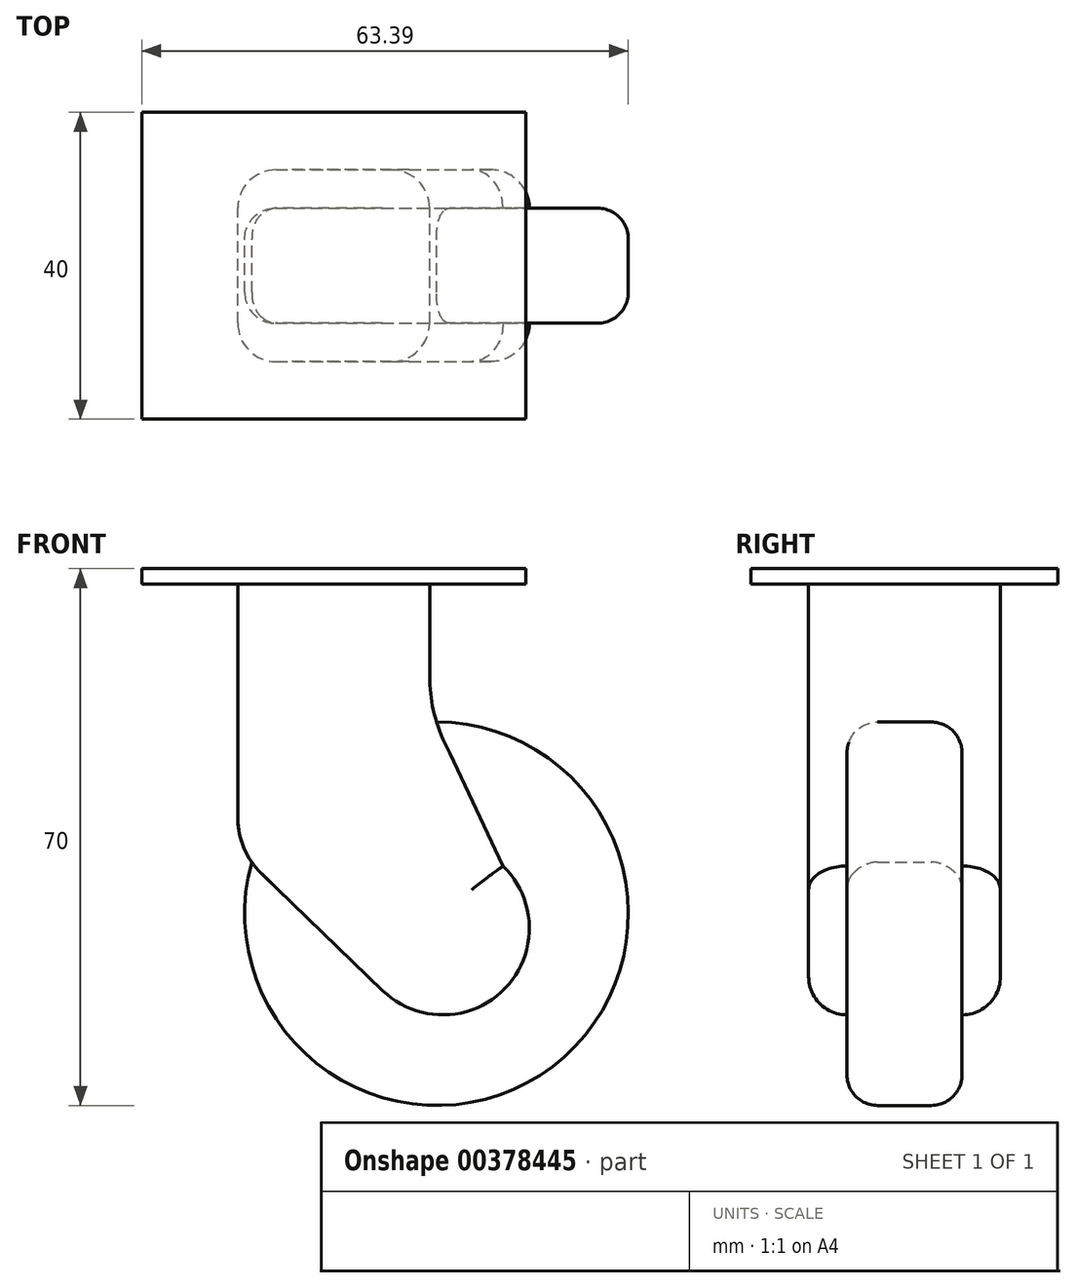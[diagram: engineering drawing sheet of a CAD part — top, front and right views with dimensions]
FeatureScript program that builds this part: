
annotation { "Feature Type Name" : "Feature", "Feature Type Description" : "" }
export const myFeature = defineFeature(function(context is Context, id is Id, definition is map)
    precondition{}
    {
        {
            var Q0;
            Q0=qCreatedBy(makeId("Top.planeOp"),FACE);
            var sketch = newSketch(context, id + "F0", { "sketchPlane" : qUnion([Q0])});
            skLineSegment(sketch, "E0.bottom", {"start": v(25, 20) * mm, "end": v(-25, 20) * mm});
            skLineSegment(sketch, "E0.top", {"start": v(25, -20) * mm, "end": v(-25, -20) * mm});
            skLineSegment(sketch, "E0.left", {"start": v(25, 20) * mm, "end": v(25, -20) * mm});
            skLineSegment(sketch, "E0.right", {"start": v(-25, 20) * mm, "end": v(-25, -20) * mm});
            skPoint(sketch, "E0.middle", {"position": v(0, 0) * mm});
            skSolve(sketch);
        }
        {
            var Q0;
            Q0=makeQuery(id+"F0.imprint","IMPRINT",FACE,{"disambiguationData":[TD([[makeQuery(id+"F0.imprint","IMPRINT",EDGE,{"derivedFrom":sQuery(id+"F0.wireOp",EDGE,"E0.bottom")}),1.0]])]});
            extrude(context, id + "F1", {"entities" : qUnion([Q0]), "depth" : 2 * mm});
        }
        {
            var Q0;
            Q0=qCreatedBy(makeId("Front.planeOp"),FACE);
            var sketch = newSketch(context, id + "F2", { "sketchPlane" : qUnion([Q0])});
            skLineSegment(sketch, "E1", {"start": v(-12.5, 0) * mm, "end": v(-12.5, -30.53) * mm});
            skLineSegment(sketch, "E2", {"start": v(12.5, 0) * mm, "end": v(12.5, -12.08) * mm});
            skLineSegment(sketch, "E3", {"start": v(14.42, -20.63) * mm, "end": v(22.05, -36.78) * mm});
            skLineSegment(sketch, "E4", {"start": v(6.35, -53) * mm, "end": v(-9.45, -37.71) * mm});
            skArc(sketch, "E5", {"start": v(6.35, -53) * mm, "mid": v(22.32, -52.75) * mm, "end": v(22.05, -36.78) * mm});
            skLineSegment(sketch, "E6", {"start": v(6.35, -53) * mm, "end": v(22.05, -36.78) * mm, "construction": true});
            skLineSegment(sketch, "E7", {"start": v(0, 0) * mm, "end": v(0, -14.48) * mm, "construction": true});
            skPoint(sketch, "E8.visualSharp", {"position": v(12.5, -16.57) * mm});
            skArc(sketch, "E8.filletArc", {"start": v(12.5, -12.08) * mm, "mid": v(12.99, -16.46) * mm, "end": v(14.42, -20.63) * mm});
            skPoint(sketch, "E9.visualSharp", {"position": v(-12.5, -34.77) * mm});
            skArc(sketch, "E9.filletArc", {"start": v(-12.5, -30.53) * mm, "mid": v(-11.7, -34.43) * mm, "end": v(-9.45, -37.71) * mm});
            skLineSegment(sketch, "E10", {"start": v(-12.5, 0) * mm, "end": v(12.5, 0) * mm});
            skSolve(sketch);
        }
        {
            var Q0;
            Q0=makeQuery(id+"F2.imprint","IMPRINT",FACE,{"disambiguationData":[TD([[makeQuery(id+"F2.imprint","IMPRINT",EDGE,{"derivedFrom":sQuery(id+"F2.wireOp",EDGE,"E1")}),1.0]])]});
            extrude(context, id + "F3", {"entities" : qUnion([Q0]), "operationType" : NewBodyOperationType.ADD, "endBound" : BoundingType.SYMMETRIC, "depth" : 25 * mm});
        }
        {
            var Q0;
            Q0=qCreatedBy(makeId("Front.planeOp"),FACE);
            var sketch = newSketch(context, id + "F4", { "sketchPlane" : qUnion([Q0])});
            skCircle(sketch, "E11", {"center": v(13.4, -43) * mm, "radius": 25 * mm});
            skSolve(sketch);
        }
        {
            var Q0;
            Q0=makeQuery(id+"F4.imprint","IMPRINT",FACE,{"disambiguationData":[TD([[makeQuery(id+"F4.imprint","IMPRINT",EDGE,{"derivedFrom":sQuery(id+"F4.wireOp",EDGE,"E11")}),1.0]])]});
            extrude(context, id + "F5", {"entities" : qUnion([Q0]), "operationType" : NewBodyOperationType.ADD, "endBound" : BoundingType.SYMMETRIC, "depth" : 15 * mm});
        }
        {
            var Q0;
            Q0=makeQuery(id+"F5.opExtrude","CAP_EDGE",EDGE,{"disambiguationData":[OSD([sQuery(id+"F4.wireOp",EDGE,"E11")])],"isStart":false});
            var Q1;
            Q1=makeQuery(id+"F5.opExtrude","CAP_EDGE",EDGE,{"disambiguationData":[OSD([sQuery(id+"F4.wireOp",EDGE,"E11")])],"isStart":true});
            fillet(context, id + "F6", {"entities" : qUnion([Q0, Q1]), "radius" : 4 * mm, "tangentPropagation" : true, "allowEdgeOverflow" : false});
        }
        {
            var Q0;
            Q0=makeQuery(id+"F3.opExtrude","CAP_EDGE",EDGE,{"disambiguationData":[OSD([sQuery(id+"F2.wireOp",EDGE,"E2")])],"isStart":false});
            var Q1;
            Q1=makeQuery(id+"F3.opExtrude","CAP_EDGE",EDGE,{"disambiguationData":[OSD([sQuery(id+"F2.wireOp",EDGE,"E1")])],"isStart":false});
            var Q2;
            Q2=makeQuery(id+"F3.opExtrude","CAP_EDGE",EDGE,{"disambiguationData":[OSD([sQuery(id+"F2.wireOp",EDGE,"E1")])],"isStart":true});
            var Q3;
            Q3=makeQuery(id+"F3.opExtrude","CAP_EDGE",EDGE,{"disambiguationData":[OSD([sQuery(id+"F2.wireOp",EDGE,"E2")])],"isStart":true});
            fillet(context, id + "F7", {"entities" : qUnion([Q0, Q1, Q2, Q3]), "radius" : 5 * mm, "tangentPropagation" : true, "allowEdgeOverflow" : false});
        }
    });
